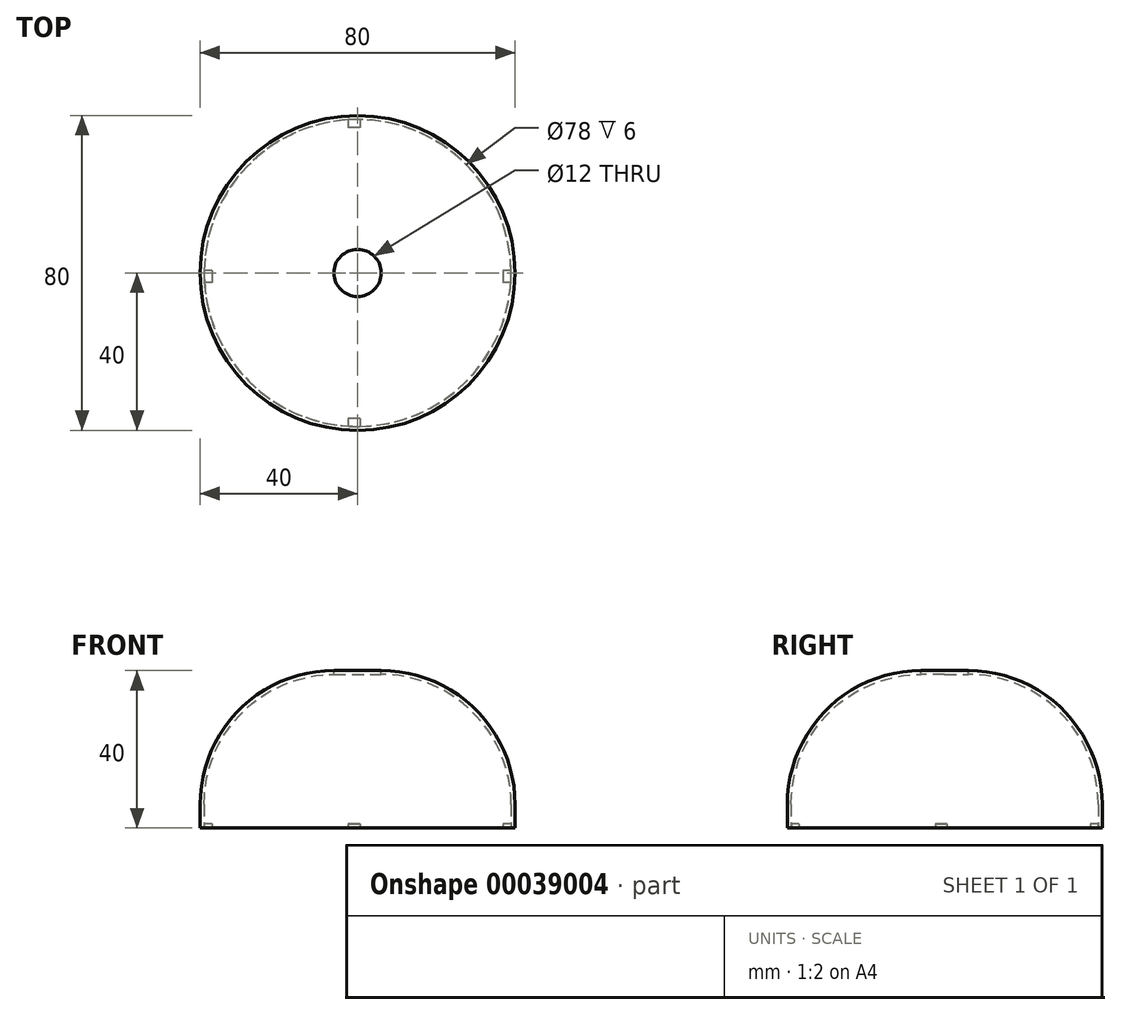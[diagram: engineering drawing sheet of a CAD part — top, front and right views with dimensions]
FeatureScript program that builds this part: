
annotation { "Feature Type Name" : "Feature", "Feature Type Description" : "" }
export const myFeature = defineFeature(function(context is Context, id is Id, definition is map)
    precondition{}
    {
        {
            var Q0;
            Q0=qCreatedBy(makeId("Top.planeOp"),FACE);
            var sketch = newSketch(context, id + "F0", { "sketchPlane" : qUnion([Q0])});
            skCircle(sketch, "E0", {"center": v(0, 0) * mm, "radius": 40 * mm});
            skLineSegment(sketch, "E1.rect.bottom", {"start": v(40, 0.6) * mm, "end": v(37, 0.6) * mm});
            skLineSegment(sketch, "E1.rect.top", {"start": v(39.93, -2.4) * mm, "end": v(37, -2.4) * mm});
            skLineSegment(sketch, "E2.rect.left", {"start": v(-2.4, 39.93) * mm, "end": v(-2.4, 37) * mm});
            skLineSegment(sketch, "E2.rect.right", {"start": v(0.6, 40) * mm, "end": v(0.6, 37) * mm});
            skLineSegment(sketch, "E3", {"start": v(37, 0.6) * mm, "end": v(37, -2.4) * mm});
            skLineSegment(sketch, "E4", {"start": v(0.6, -37) * mm, "end": v(-2.4, -37) * mm});
            skLineSegment(sketch, "E5", {"start": v(-37, 0.6) * mm, "end": v(-37, -2.4) * mm});
            skLineSegment(sketch, "E6", {"start": v(0.6, 37) * mm, "end": v(-2.4, 37) * mm});
            skLineSegment(sketch, "E7.trimOffspring", {"start": v(-37, 0.6) * mm, "end": v(-40, 0.6) * mm});
            skLineSegment(sketch, "E8.trimOffspring", {"start": v(-37, -2.4) * mm, "end": v(-39.93, -2.4) * mm});
            skLineSegment(sketch, "E9.trimOffspring", {"start": v(-2.4, -37) * mm, "end": v(-2.4, -39.93) * mm});
            skLineSegment(sketch, "E10", {"start": v(0.6, -37) * mm, "end": v(0.6, -40) * mm});
            skSolve(sketch);
        }
        {
            var Q0;
            {var subQ0=sQuery(id+"F0.wireOp",EDGE,"E2.rect.right");var subQ4=sQuery(id+"F0.wireOp",EDGE,"E0");var subQ6=makeQuery(id+"F0.imprint","INTERSECT",VERTEX,{"disambiguationData":[OD(0.0)],"derivedFrom":[subQ4,subQ0]});Q0=makeQuery(id+"F0.imprint","IMPRINT",FACE,{"disambiguationData":[TD([[makeQuery(id+"F0.imprint","IMPRINT",EDGE,{"disambiguationData":[TD([[subQ6,1.0]])],"derivedFrom":subQ4}),1.0]])]});}
            var Q1;
            {var subQ1=sQuery(id+"F0.wireOp",EDGE,"E0");var subQ4=sQuery(id+"F0.wireOp",EDGE,"E2.rect.right");var subQ5=makeQuery(id+"F0.imprint","INTERSECT",VERTEX,{"disambiguationData":[OD(1.0)],"derivedFrom":[subQ1,subQ4]});Q1=makeQuery(id+"F0.imprint","IMPRINT",FACE,{"disambiguationData":[TD([[makeQuery(id+"F0.imprint","IMPRINT",EDGE,{"disambiguationData":[TD([[subQ5,-1.0]])],"derivedFrom":subQ1}),1.0]])]});}
            var Q2;
            {var subQ1=sQuery(id+"F0.wireOp",EDGE,"E0");var subQ4=sQuery(id+"F0.wireOp",EDGE,"E1.rect.top");var subQ5=makeQuery(id+"F0.imprint","INTERSECT",VERTEX,{"disambiguationData":[OD(0.0)],"derivedFrom":[subQ1,subQ4]});Q2=makeQuery(id+"F0.imprint","IMPRINT",FACE,{"disambiguationData":[TD([[makeQuery(id+"F0.imprint","IMPRINT",EDGE,{"disambiguationData":[TD([[subQ5,-1.0]])],"derivedFrom":subQ1}),1.0]])]});}
            var Q3;
            {var subQ0=sQuery(id+"F0.wireOp",EDGE,"E2.rect.left");var subQ4=sQuery(id+"F0.wireOp",EDGE,"E0");var subQ6=makeQuery(id+"F0.imprint","INTERSECT",VERTEX,{"disambiguationData":[OD(0.0)],"derivedFrom":[subQ4,subQ0]});Q3=makeQuery(id+"F0.imprint","IMPRINT",FACE,{"disambiguationData":[TD([[makeQuery(id+"F0.imprint","IMPRINT",EDGE,{"disambiguationData":[TD([[subQ6,-1.0]])],"derivedFrom":subQ4}),1.0]])]});}
            var Q4;
            {var subQ5=sQuery(id+"F0.wireOp",EDGE,"E3");Q4=makeQuery(id+"F0.imprint","IMPRINT",FACE,{"disambiguationData":[TD([[makeQuery(id+"F0.imprint","IMPRINT",EDGE,{"derivedFrom":subQ5}),-1.0]])]});}
            var Q5;
            {var subQ3=sQuery(id+"F0.wireOp",EDGE,"E5");Q5=makeQuery(id+"F0.imprint","IMPRINT",FACE,{"disambiguationData":[TD([[makeQuery(id+"F0.imprint","IMPRINT",EDGE,{"derivedFrom":subQ3}),1.0]])]});}
            var Q6;
            {var subQ3=sQuery(id+"F0.wireOp",EDGE,"E3");Q6=makeQuery(id+"F0.imprint","IMPRINT",FACE,{"disambiguationData":[TD([[makeQuery(id+"F0.imprint","IMPRINT",EDGE,{"derivedFrom":subQ3}),1.0]])]});}
            var Q7;
            {var subQ0=sQuery(id+"F0.wireOp",EDGE,"E4");Q7=makeQuery(id+"F0.imprint","IMPRINT",FACE,{"disambiguationData":[TD([[makeQuery(id+"F0.imprint","IMPRINT",EDGE,{"derivedFrom":subQ0}),1.0]])]});}
            var Q8;
            {var subQ3=sQuery(id+"F0.wireOp",EDGE,"E5");Q8=makeQuery(id+"F0.imprint","IMPRINT",FACE,{"disambiguationData":[TD([[makeQuery(id+"F0.imprint","IMPRINT",EDGE,{"derivedFrom":subQ3}),-1.0]])]});}
            var Q9;
            {var subQ3=sQuery(id+"F0.wireOp",EDGE,"E6");Q9=makeQuery(id+"F0.imprint","IMPRINT",FACE,{"disambiguationData":[TD([[makeQuery(id+"F0.imprint","IMPRINT",EDGE,{"derivedFrom":subQ3}),-1.0]])]});}
            var Q10;
            {var subQ3=sQuery(id+"F0.wireOp",EDGE,"E6");Q10=makeQuery(id+"F0.imprint","IMPRINT",FACE,{"disambiguationData":[TD([[makeQuery(id+"F0.imprint","IMPRINT",EDGE,{"derivedFrom":subQ3}),1.0]])]});}
            var Q11;
            {var subQ0=sQuery(id+"F0.wireOp",EDGE,"E2.rect.right");var subQ3=sQuery(id+"F0.wireOp",EDGE,"E1.rect.bottom");var subQ4=makeQuery(id+"F0.imprint","INTERSECT",VERTEX,{"derivedFrom":[subQ3,subQ0]});Q11=makeQuery(id+"F0.imprint","IMPRINT",FACE,{"disambiguationData":[TD([[makeQuery(id+"F0.imprint","IMPRINT",EDGE,{"disambiguationData":[TD([[subQ4,-1.0]])],"derivedFrom":subQ3}),1.0]])]});}
            var Q12;
            {var subQ0=sQuery(id+"F0.wireOp",EDGE,"E4");Q12=makeQuery(id+"F0.imprint","IMPRINT",FACE,{"disambiguationData":[TD([[makeQuery(id+"F0.imprint","IMPRINT",EDGE,{"derivedFrom":subQ0}),-1.0]])]});}
            extrude(context, id + "F1", {"entities" : qUnion([Q0, Q1, Q2, Q3, Q4, Q5, Q6, Q7, Q8, Q9, Q10, Q11, Q12]), "depth" : 40 * mm});
        }
        {
            var Q0;
            Q0=makeQuery(id+"F1.opExtrude","CAP_EDGE",EDGE,{"disambiguationData":[OSD([sQuery(id+"F0.wireOp",EDGE,"E0")])],"isStart":false});
            fillet(context, id + "F2", {"entities" : qUnion([Q0]), "radius" : 34 * mm, "tangentPropagation" : true, "allowEdgeOverflow" : false});
        }
        {
            var Q0;
            Q0=makeQuery(id+"F1.opExtrude","CAP_FACE",FACE,{"disambiguationData":[OSD([sQuery(id+"F0.wireOp",EDGE,"E0")])],"isStart":false});
            var Q1;
            Q1=makeQuery(id+"F1.opExtrude","CAP_FACE",FACE,{"disambiguationData":[OSD([sQuery(id+"F0.wireOp",EDGE,"E0")])],"isStart":true});
            shell(context, id + "F3", {"entities" : qUnion([Q0, Q1]), "thickness" : 1 * mm});
        }
        {
            var Q0;
            {var subQ3=sQuery(id+"F0.wireOp",EDGE,"E3");Q0=makeQuery(id+"F0.imprint","IMPRINT",FACE,{"disambiguationData":[TD([[makeQuery(id+"F0.imprint","IMPRINT",EDGE,{"derivedFrom":subQ3}),1.0]])]});}
            var Q1;
            {var subQ3=sQuery(id+"F0.wireOp",EDGE,"E6");Q1=makeQuery(id+"F0.imprint","IMPRINT",FACE,{"disambiguationData":[TD([[makeQuery(id+"F0.imprint","IMPRINT",EDGE,{"derivedFrom":subQ3}),-1.0]])]});}
            var Q2;
            {var subQ3=sQuery(id+"F0.wireOp",EDGE,"E5");Q2=makeQuery(id+"F0.imprint","IMPRINT",FACE,{"disambiguationData":[TD([[makeQuery(id+"F0.imprint","IMPRINT",EDGE,{"derivedFrom":subQ3}),-1.0]])]});}
            var Q3;
            {var subQ0=sQuery(id+"F0.wireOp",EDGE,"E4");Q3=makeQuery(id+"F0.imprint","IMPRINT",FACE,{"disambiguationData":[TD([[makeQuery(id+"F0.imprint","IMPRINT",EDGE,{"derivedFrom":subQ0}),1.0]])]});}
            extrude(context, id + "F4", {"entities" : qUnion([Q0, Q1, Q2, Q3]), "operationType" : NewBodyOperationType.ADD, "depth" : 1 * mm});
        }
    });
